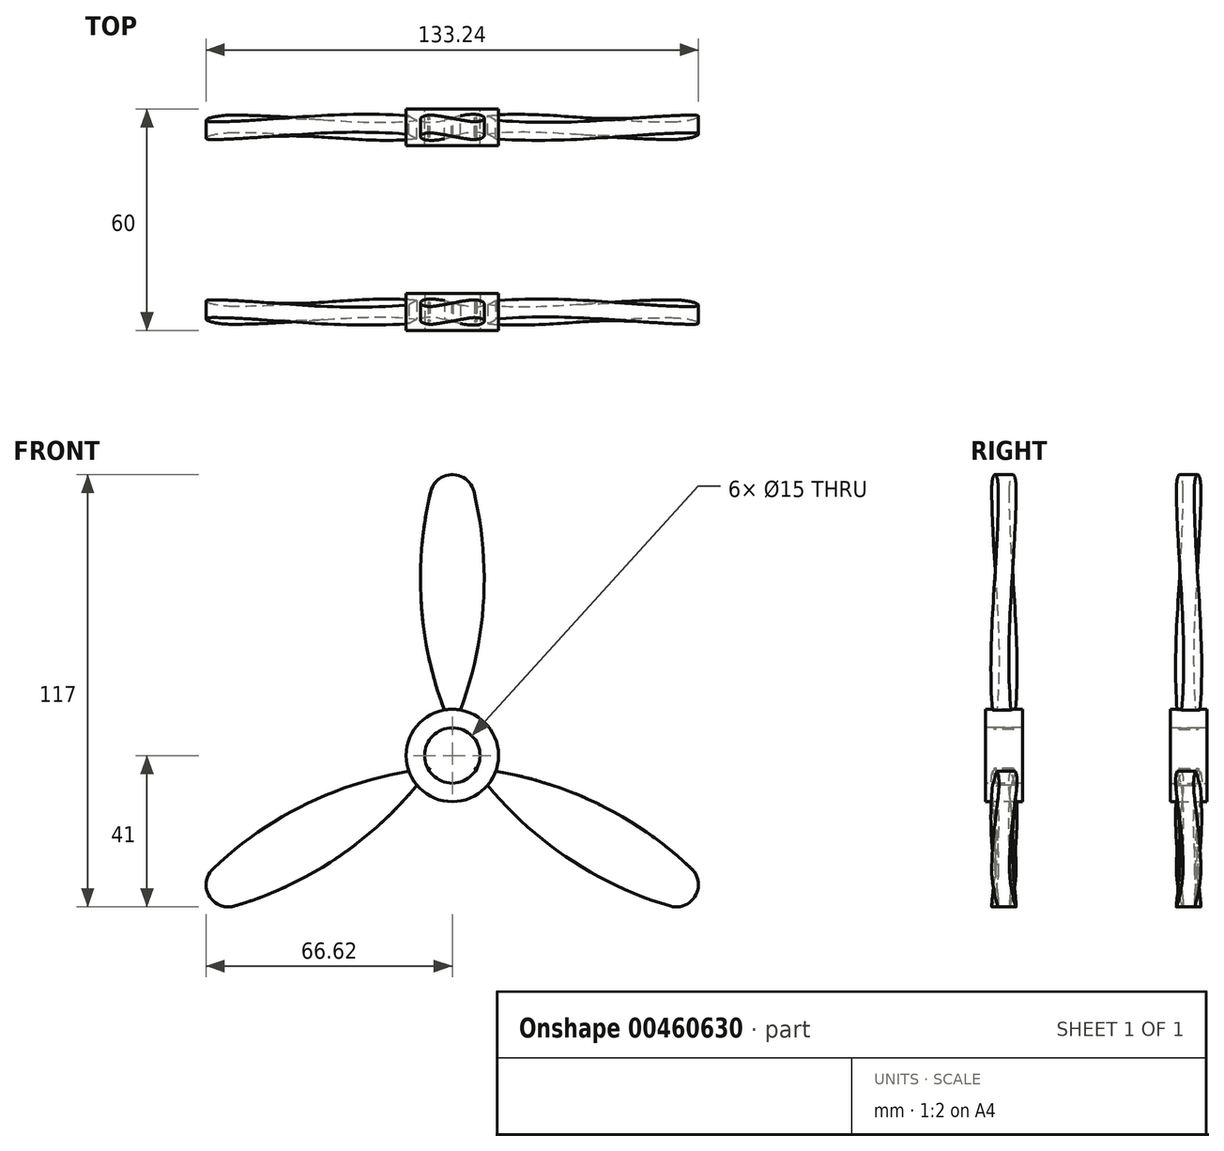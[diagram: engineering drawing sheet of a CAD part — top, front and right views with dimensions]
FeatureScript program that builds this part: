
annotation { "Feature Type Name" : "Feature", "Feature Type Description" : "" }
export const myFeature = defineFeature(function(context is Context, id is Id, definition is map)
    precondition{}
    {
        {
            var Q0;
            Q0=qCreatedBy(makeId("Top.planeOp"),FACE);
            cPlane(context, id + "F0", {"entities" : qUnion([Q0]), "cplaneType" : CPlaneType.OFFSET, "offset" : 100 * mm, "width" : 150 * mm, "height" : 150 * mm});
        }
        {
            var Q0;
            Q0=qCreatedBy(makeId("Top.planeOp"),FACE);
            var sketch = newSketch(context, id + "F1", { "sketchPlane" : qUnion([Q0])});
            skLineSegment(sketch, "E0", {"start": v(0, 59.5) * mm, "end": v(0, -61.17) * mm, "construction": true});
            skLineSegment(sketch, "E1", {"start": v(45.37, 0) * mm, "end": v(-60.34, 0) * mm, "construction": true});
            skLineSegment(sketch, "E2", {"start": v(-22.64, -10.9) * mm, "end": v(24.35, 6.2) * mm});
            skLineSegment(sketch, "E3", {"start": v(24.35, 6.2) * mm, "end": v(22.64, 10.9) * mm});
            skLineSegment(sketch, "E4", {"start": v(22.64, 10.9) * mm, "end": v(-24.35, -6.2) * mm});
            skLineSegment(sketch, "E5", {"start": v(-24.35, -6.2) * mm, "end": v(-22.64, -10.9) * mm});
            skLineSegment(sketch, "E6", {"start": v(23.5, 8.55) * mm, "end": v(-23.5, -8.55) * mm, "construction": true});
            skLineSegment(sketch, "E7", {"start": v(0.86, -2.35) * mm, "end": v(-0.86, 2.35) * mm, "construction": true});
            skSolve(sketch);
        }
        {
            var Q0;
            Q0=qCreatedBy(id+"F0.planeOp",FACE);
            var sketch = newSketch(context, id + "F2", { "sketchPlane" : qUnion([Q0])});
            skLineSegment(sketch, "E8", {"start": v(0, 24.82) * mm, "end": v(0, -29.1) * mm, "construction": true});
            skLineSegment(sketch, "E9", {"start": v(-37.06, 0) * mm, "end": v(34.92, 0) * mm, "construction": true});
            skLineSegment(sketch, "E10", {"start": v(-24.35, 6.2) * mm, "end": v(22.64, -10.9) * mm});
            skLineSegment(sketch, "E11", {"start": v(22.64, -10.9) * mm, "end": v(24.35, -6.2) * mm});
            skLineSegment(sketch, "E12", {"start": v(24.35, -6.2) * mm, "end": v(-22.64, 10.9) * mm});
            skLineSegment(sketch, "E13", {"start": v(-22.64, 10.9) * mm, "end": v(-24.35, 6.2) * mm});
            skLineSegment(sketch, "E14", {"start": v(-23.5, 8.55) * mm, "end": v(23.5, -8.55) * mm, "construction": true});
            skLineSegment(sketch, "E15", {"start": v(-0.86, -2.35) * mm, "end": v(0.86, 2.35) * mm, "construction": true});
            skSolve(sketch);
        }
        {
            var Q0;
            Q0=makeQuery(id+"F2.imprint","IMPRINT",FACE,{"disambiguationData":[TD([[makeQuery(id+"F2.imprint","IMPRINT",EDGE,{"derivedFrom":sQuery(id+"F2.wireOp",EDGE,"E10")}),1.0]])]});
            var Q1;
            Q1=makeQuery(id+"F1.imprint","IMPRINT",FACE,{"disambiguationData":[TD([[makeQuery(id+"F1.imprint","IMPRINT",EDGE,{"derivedFrom":sQuery(id+"F1.wireOp",EDGE,"E2")}),1.0]])]});
            loft(context, id + "F3", {"sheetProfilesArray" : [{ "sheetProfileEntities" : qUnion([Q0]) }, { "sheetProfileEntities" : qUnion([Q1]) }]});
        }
        {
            var Q0;
            Q0=qCreatedBy(makeId("Front.planeOp"),FACE);
            var sketch = newSketch(context, id + "F4", { "sketchPlane" : qUnion([Q0])});
            skLineSegment(sketch, "E16", {"start": v(0, 0) * mm, "end": v(0, 133.08) * mm, "construction": true});
            skArc(sketch, "E17", {"start": v(0, 7) * mm, "mid": v(8.22, 38.72) * mm, "end": v(5.83, 71.4) * mm});
            skArc(sketch, "E18", {"start": v(5.83, 71.4) * mm, "mid": v(3.71, 74.71) * mm, "end": v(0, 76) * mm});
            skArc(sketch, "E19.MirrorCS", {"start": v(-5.83, 71.4) * mm, "mid": v(-3.71, 74.71) * mm, "end": v(0, 76) * mm});
            skArc(sketch, "E20.MirrorCS", {"start": v(0, 7) * mm, "mid": v(-8.22, 38.72) * mm, "end": v(-5.83, 71.4) * mm});
            skSolve(sketch);
        }
        {
            var Q0;
            Q0 = qSketchRegion(id + "F4", true);
            extrude(context, id + "F5", {"entities" : qUnion([Q0]), "operationType" : NewBodyOperationType.INTERSECT, "endBound" : BoundingType.SYMMETRIC, "depth" : 20 * mm});
        }
        {
            var Q0;
            Q0=qCreatedBy(makeId("Front.planeOp"),FACE);
            var sketch = newSketch(context, id + "F6", { "sketchPlane" : qUnion([Q0])});
            skCircle(sketch, "E21", {"center": v(0, 0) * mm, "radius": 12.5 * mm});
            skCircle(sketch, "E22", {"center": v(0, 0) * mm, "radius": 7.5 * mm});
            skSolve(sketch);
        }
        {
            var Q0;
            Q0=makeQuery(id+"F6.imprint","IMPRINT",FACE,{"disambiguationData":[TD([[makeQuery(id+"F6.imprint","IMPRINT",EDGE,{"derivedFrom":sQuery(id+"F6.wireOp",EDGE,"E21")}),1.0]])]});
            extrude(context, id + "F7", {"entities" : qUnion([Q0]), "operationType" : NewBodyOperationType.ADD, "endBound" : BoundingType.SYMMETRIC, "depth" : 10 * mm});
        }
        {
            var Q0;
            Q0=makeQuery(id+"F3.opLoft","SWEPT_BODY",BODY,{"disambiguationData":[OSD([makeQuery(id+"F1.imprint","IMPRINT",FACE,{"disambiguationData":[TD([[makeQuery(id+"F1.imprint","IMPRINT",EDGE,{"derivedFrom":sQuery(id+"F1.wireOp",EDGE,"E2")}),1.0]])]}),makeQuery(id+"F2.imprint","IMPRINT",FACE,{"disambiguationData":[TD([[makeQuery(id+"F2.imprint","IMPRINT",EDGE,{"derivedFrom":sQuery(id+"F2.wireOp",EDGE,"E10")}),1.0]])]})])]});
            var Q1;
            Q1=makeQuery(id+"F7.opExtrude","CAP_EDGE",EDGE,{"disambiguationData":[OSD([sQuery(id+"F6.wireOp",EDGE,"E22")])],"isStart":false});
            circularPattern(context, id + "F8", {"entities" : qUnion([Q0]), "axis" : qUnion([Q1]), "angle" : 360 * degree, "instanceCount" : 3, "equalSpace" : true});
        }
        {
            var Q0;
            Q0=qCreatedBy(makeId("Front.planeOp"),FACE);
            cPlane(context, id + "F9", {"entities" : qUnion([Q0]), "cplaneType" : CPlaneType.OFFSET, "offset" : 25 * mm, "width" : 150 * mm, "height" : 150 * mm});
        }
        {
            var Q0;
            Q0=makeQuery(id+"F3.opLoft","SWEPT_BODY",BODY,{"disambiguationData":[OSD([makeQuery(id+"F1.imprint","IMPRINT",FACE,{"disambiguationData":[TD([[makeQuery(id+"F1.imprint","IMPRINT",EDGE,{"derivedFrom":sQuery(id+"F1.wireOp",EDGE,"E2")}),1.0]])]}),makeQuery(id+"F2.imprint","IMPRINT",FACE,{"disambiguationData":[TD([[makeQuery(id+"F2.imprint","IMPRINT",EDGE,{"derivedFrom":sQuery(id+"F2.wireOp",EDGE,"E10")}),1.0]])]})])]});
            var Q1;
            Q1=makeQuery(id+"F8.opPattern","COPY",BODY,{"derivedFrom":makeQuery(id+"F3.opLoft","SWEPT_BODY",BODY,{"disambiguationData":[OSD([makeQuery(id+"F1.imprint","IMPRINT",FACE,{"disambiguationData":[TD([[makeQuery(id+"F1.imprint","IMPRINT",EDGE,{"derivedFrom":sQuery(id+"F1.wireOp",EDGE,"E2")}),1.0]])]}),makeQuery(id+"F2.imprint","IMPRINT",FACE,{"disambiguationData":[TD([[makeQuery(id+"F2.imprint","IMPRINT",EDGE,{"derivedFrom":sQuery(id+"F2.wireOp",EDGE,"E10")}),1.0]])]})])]}),"instanceName":"2"});
            var Q2;
            Q2=makeQuery(id+"F8.opPattern","COPY",BODY,{"derivedFrom":makeQuery(id+"F3.opLoft","SWEPT_BODY",BODY,{"disambiguationData":[OSD([makeQuery(id+"F1.imprint","IMPRINT",FACE,{"disambiguationData":[TD([[makeQuery(id+"F1.imprint","IMPRINT",EDGE,{"derivedFrom":sQuery(id+"F1.wireOp",EDGE,"E2")}),1.0]])]}),makeQuery(id+"F2.imprint","IMPRINT",FACE,{"disambiguationData":[TD([[makeQuery(id+"F2.imprint","IMPRINT",EDGE,{"derivedFrom":sQuery(id+"F2.wireOp",EDGE,"E10")}),1.0]])]})])]}),"instanceName":"1"});
            var Q3;
            Q3=qCreatedBy(id+"F9.planeOp",FACE);
            mirror(context, id + "F10", {"entities" : qUnion([Q0, Q1, Q2]), "mirrorPlane" : qUnion([Q3])});
        }
    });
